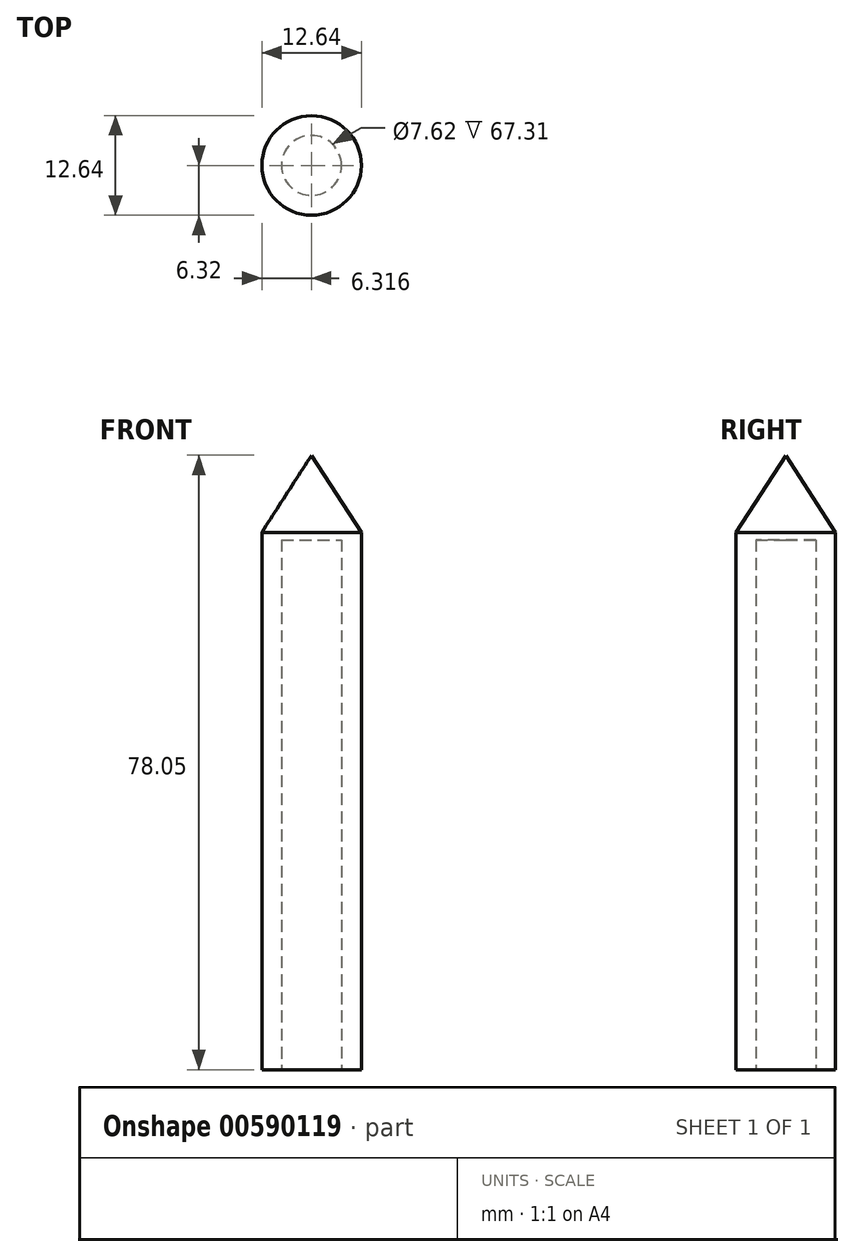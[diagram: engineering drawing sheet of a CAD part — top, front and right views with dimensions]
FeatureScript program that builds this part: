
annotation { "Feature Type Name" : "Feature", "Feature Type Description" : "" }
export const myFeature = defineFeature(function(context is Context, id is Id, definition is map)
    precondition{}
    {
        {
            var Q0;
            Q0=qCreatedBy(makeId("Front.planeOp"),FACE);
            var sketch = newSketch(context, id + "F0", { "sketchPlane" : qUnion([Q0])});
            skLineSegment(sketch, "E0", {"start": v(-51.03, 67.35) * mm, "end": v(-51.03, -10.7) * mm});
            skLineSegment(sketch, "E1", {"start": v(-51.03, -10.7) * mm, "end": v(-44.71, -10.7) * mm});
            skLineSegment(sketch, "E2", {"start": v(-44.71, -10.7) * mm, "end": v(-44.71, 57.55) * mm});
            skLineSegment(sketch, "E3", {"start": v(-44.71, 57.55) * mm, "end": v(-51.03, 67.35) * mm});
            skSolve(sketch);
        }
        {
            var Q0;
            Q0 = qSketchRegion(id + "F0", true);
            var Q1;
            Q1=sQuery(id+"F0.wireOp",EDGE,"E0");
            revolve(context, id + "F1", {"entities" : qUnion([Q0]), "axis" : qUnion([Q1]), "revolveType" : RevolveType.FULL});
        }
        {
            var Q0;
            Q0=makeQuery(id+"F1.opRevolve","SWEPT_FACE",FACE,{"disambiguationData":[OSD([sQuery(id+"F0.wireOp",EDGE,"E1")])]});
            var sketch = newSketch(context, id + "F2", { "sketchPlane" : qUnion([Q0])});
            skCircle(sketch, "E4", {"center": v(-51.03, 0) * mm, "radius": 3.8 * mm});
            skSolve(sketch);
        }
        {
            var Q0;
            Q0 = qSketchRegion(id + "F2", true);
            extrude(context, id + "F3", {"entities" : qUnion([Q0]), "operationType" : NewBodyOperationType.REMOVE, "oppositeDirection" : true, "depth" : 67.3 * mm, "offsetDistance" : 25.4 * mm});
        }
    });
